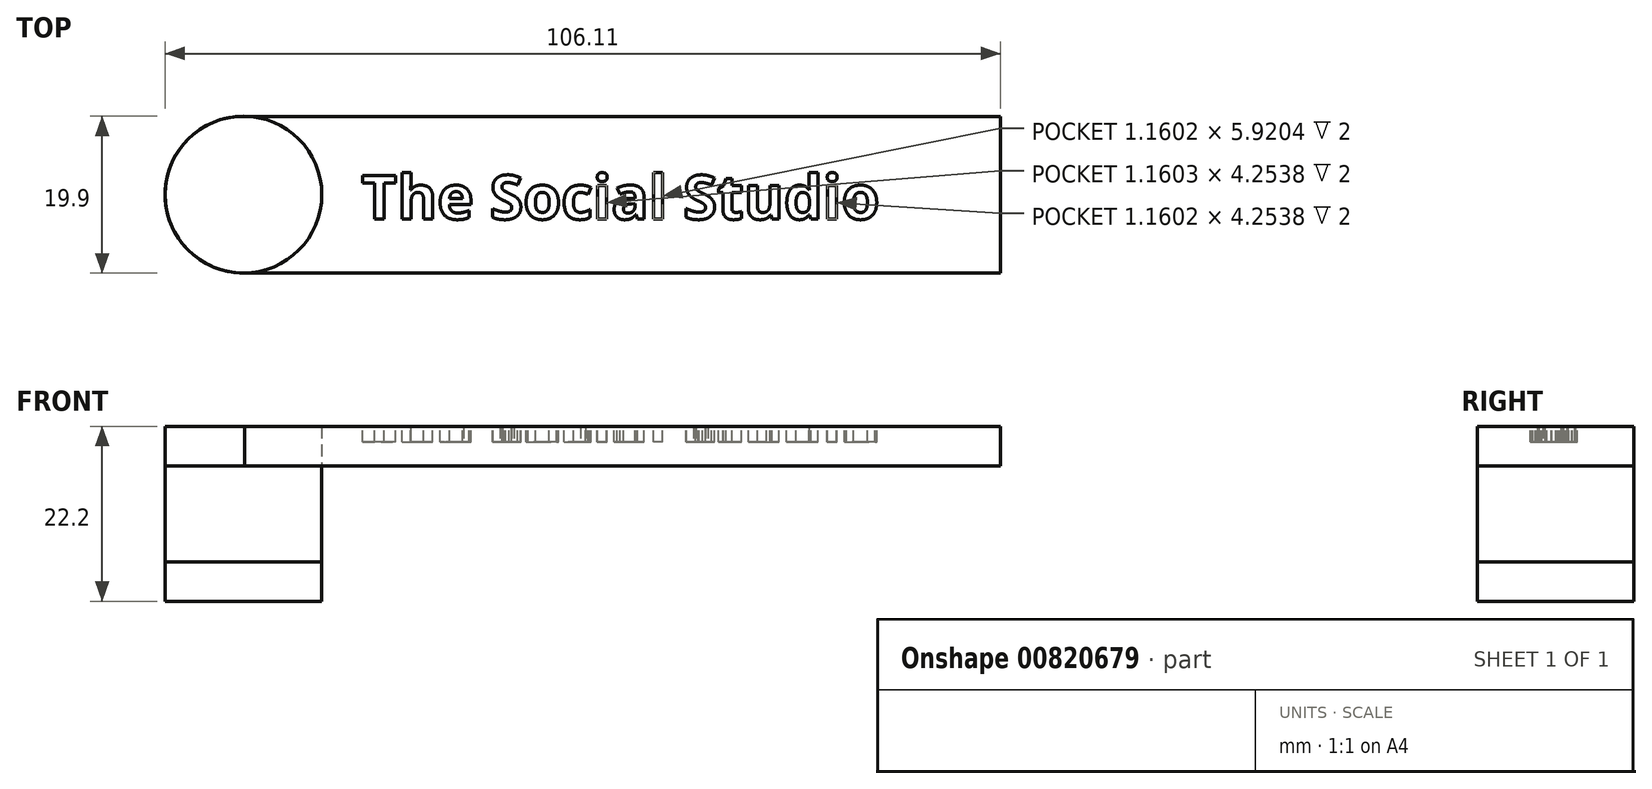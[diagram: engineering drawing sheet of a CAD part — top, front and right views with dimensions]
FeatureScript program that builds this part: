
annotation { "Feature Type Name" : "Feature", "Feature Type Description" : "" }
export const myFeature = defineFeature(function(context is Context, id is Id, definition is map)
    precondition{}
    {
        {
            var Q0;
            Q0=qCreatedBy(makeId("Top.planeOp"),FACE);
            var sketch = newSketch(context, id + "F0", { "sketchPlane" : qUnion([Q0])});
            skCircle(sketch, "E0", {"center": v(-48, 0) * mm, "radius": 9.95 * mm});
            skCircle(sketch, "E1.MirrorC", {"center": v(48, 0) * mm, "radius": 9.95 * mm});
            skLineSegment(sketch, "E2", {"start": v(47.8, 9.95) * mm, "end": v(48, -9.95) * mm, "construction": true});
            skLineSegment(sketch, "E3", {"start": v(-48.1, 9.95) * mm, "end": v(-48.1, -9.95) * mm, "construction": true});
            skSolve(sketch);
        }
        {
            var Q0;
            Q0=makeQuery(id+"F0.imprint","IMPRINT",FACE,{"disambiguationData":[TD([[makeQuery(id+"F0.imprint","IMPRINT",EDGE,{"derivedFrom":sQuery(id+"F0.wireOp",EDGE,"E0")}),1.0]])]});
            var Q1;
            Q1=makeQuery(id+"F0.imprint","IMPRINT",FACE,{"disambiguationData":[TD([[makeQuery(id+"F0.imprint","IMPRINT",EDGE,{"derivedFrom":sQuery(id+"F0.wireOp",EDGE,"E1.MirrorC")}),-1.0]])]});
            extrude(context, id + "F1", {"entities" : qUnion([Q0, Q1]), "depth" : 17.2 * mm, "offsetDistance" : 25 * mm});
        }
        {
            var Q0;
            Q0=makeQuery(id+"F1.opExtrude","CAP_FACE",FACE,{"disambiguationData":[OSD([sQuery(id+"F0.wireOp",EDGE,"E0")])],"isStart":false});
            var sketch = newSketch(context, id + "F2", { "sketchPlane" : qUnion([Q0])});
            skLineSegment(sketch, "E4.bottom", {"start": v(-48.16, -9.95) * mm, "end": v(48.16, -9.95) * mm});
            skLineSegment(sketch, "E4.top", {"start": v(-48.16, 9.95) * mm, "end": v(48.16, 9.95) * mm});
            skLineSegment(sketch, "E4.left", {"start": v(-48.16, -9.95) * mm, "end": v(-48.16, 9.95) * mm});
            skLineSegment(sketch, "E4.right", {"start": v(48.16, -9.95) * mm, "end": v(48.16, 9.95) * mm});
            skPoint(sketch, "E4.middle", {"position": v(0, 0) * mm});
            skSolve(sketch);
        }
        {
            var Q0;
            {var subQ0=sQuery(id+"F2.wireOp",EDGE,"E4.left");Q0=makeQuery(id+"F2.imprint","IMPRINT",FACE,{"disambiguationData":[TD([[makeQuery(id+"F2.imprint","IMPRINT",EDGE,{"derivedFrom":subQ0}),1.0]])]});}
            var Q1;
            {var subQ0=sQuery(id+"F2.wireOp",EDGE,"E4.right");Q1=makeQuery(id+"F2.imprint","IMPRINT",FACE,{"disambiguationData":[TD([[makeQuery(id+"F2.imprint","IMPRINT",EDGE,{"derivedFrom":subQ0}),1.0]])]});}
            var Q2;
            {var subQ0=sQuery(id+"F2.wireOp",EDGE,"E4.left");Q2=makeQuery(id+"F2.imprint","IMPRINT",FACE,{"disambiguationData":[TD([[makeQuery(id+"F2.imprint","IMPRINT",EDGE,{"derivedFrom":subQ0}),-1.0]])]});}
            var Q3;
            Q3=makeQuery(id+"F1.opExtrude","CAP_FACE",FACE,{"disambiguationData":[OSD([sQuery(id+"F0.wireOp",EDGE,"E1.MirrorC")])],"isStart":false});
            var Q4;
            Q4=makeQuery(id+"F1.opExtrude","CAP_FACE",FACE,{"disambiguationData":[OSD([sQuery(id+"F0.wireOp",EDGE,"E0")])],"isStart":false});
            var Q5;
            Q5=makeQuery(id+"F1.opExtrude","CAP_FACE",FACE,{"disambiguationData":[OSD([sQuery(id+"F0.wireOp",EDGE,"E1.MirrorC")])],"isStart":true});
            var Q6;
            Q6=makeQuery(id+"F1.opExtrude","CAP_FACE",FACE,{"disambiguationData":[OSD([sQuery(id+"F0.wireOp",EDGE,"E0")])],"isStart":true});
            var Q7;
            {var subQ0=sQuery(id+"F2.wireOp",EDGE,"E4.top");var subQ1=makeQuery(id+"F1.opExtrude","CAP_EDGE",EDGE,{"disambiguationData":[OSD([sQuery(id+"F0.wireOp",EDGE,"E0")])],"isStart":false});var subQ3=makeQuery(id+"F2.imprint","INTERSECT",VERTEX,{"derivedFrom":[subQ1,subQ0]});Q7=makeQuery(id+"F2.imprint","IMPRINT",FACE,{"disambiguationData":[TD([[makeQuery(id+"F2.imprint","IMPRINT",EDGE,{"disambiguationData":[TD([[subQ3,1.0]])],"derivedFrom":subQ0}),1.0]])]});}
            var Q8;
            {var subQ0=sQuery(id+"F2.wireOp",EDGE,"E4.bottom");var subQ1=makeQuery(id+"F1.opExtrude","CAP_EDGE",EDGE,{"disambiguationData":[OSD([sQuery(id+"F0.wireOp",EDGE,"E0")])],"isStart":false});var subQ3=makeQuery(id+"F2.imprint","INTERSECT",VERTEX,{"derivedFrom":[subQ1,subQ0]});Q8=makeQuery(id+"F2.imprint","IMPRINT",FACE,{"disambiguationData":[TD([[makeQuery(id+"F2.imprint","IMPRINT",EDGE,{"disambiguationData":[TD([[subQ3,1.0]])],"derivedFrom":subQ0}),-1.0]])]});}
            extrude(context, id + "F3", {"entities" : qUnion([Q0, Q1, Q2, Q3, Q4, Q5, Q6, Q7, Q8]), "depth" : 5 * mm, "offsetDistance" : 25 * mm});
        }
        {
            var Q0;
            Q0=makeQuery(id+"F3.opExtrude","CAP_FACE",FACE,{"disambiguationData":[OSD([sQuery(id+"F0.wireOp",EDGE,"E0"),sQuery(id+"F2.wireOp",EDGE,"E4.bottom"),sQuery(id+"F2.wireOp",EDGE,"E4.top"),sQuery(id+"F2.wireOp",EDGE,"E4.right")])],"isStart":false});
            var sketch = newSketch(context, id + "F4", { "sketchPlane" : qUnion([Q0])});
            skText(sketch, "E5", { "text": "The Social Studio", "fontName": "OpenSans-Bold.ttf"});
            const initialGuessF4  = {"E5": [-0.033, -0.00312, 1, 0, 0.00561]};
            skSetInitialGuess(sketch, initialGuessF4);
            skSolve(sketch);
        }
        {
            var Q0;
            Q0 = qSketchRegion(id + "F4", true);
            extrude(context, id + "F5", {"entities" : qUnion([Q0]), "operationType" : NewBodyOperationType.REMOVE, "oppositeDirection" : true, "depth" : 2 * mm, "offsetDistance" : 25 * mm});
        }
    });
